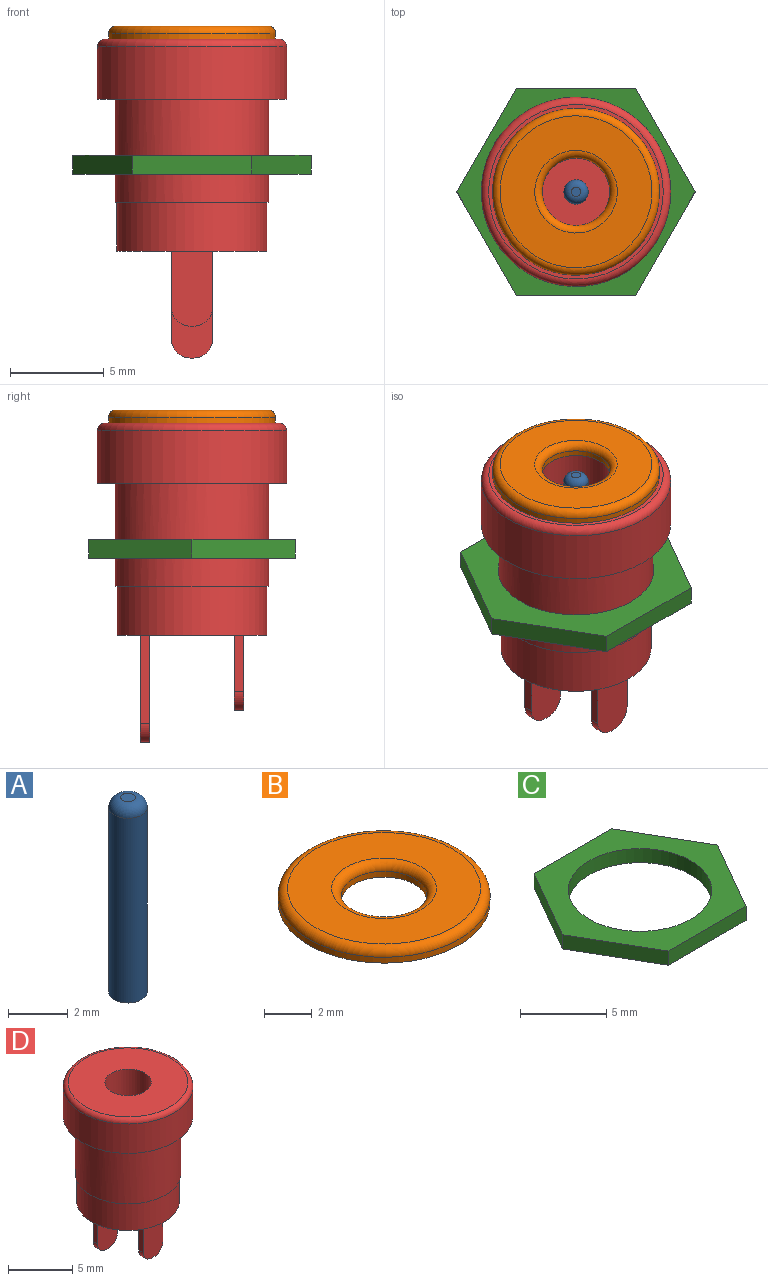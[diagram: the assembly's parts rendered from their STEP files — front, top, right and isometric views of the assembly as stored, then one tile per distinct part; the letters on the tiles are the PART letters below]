
ASSEMBLY  parts=4 mates=3
PART A: 4 faces, bbox 1.3x1.3x8 mm
  f0: cylinder r=0.65mm len=7.6mm, axis (0,0,1), area 31mm2, adj f1,f3
  f1: plane 1.3x1.3mm, normal (0,0,-1), area 1.3mm2, adj f0
  f2: plane 0.5x0.5mm, normal (0,0,1), area 0.2mm2, adj f3
  f3: torus R=0.25mm, axis (0,0,1), area 2mm2, adj f0,f2
PART B: 6 faces, bbox 9.6x9.6x0.7 mm
  f0: cylinder r=1.8mm len=3.6mm, axis (0,0,1), area 3.4mm2, adj f2,f4
  f1: cylinder r=4.45mm len=8.9mm, axis (0,0,1), area 8.4mm2, adj f2,f5
  f2: plane 8.9x8.9mm, normal (0,0,-1), area 52mm2, adj f0,f1
  f3: plane 8.1x8.1mm, normal (0,0,1), area 36.3mm2, adj f4,f5
  f4: torus R=2.2mm, axis (0,0,1), area 7.7mm2, adj f0,f3
  f5: torus R=4.05mm, axis (0,0,1), area 17mm2, adj f1,f3
PART C: 9 faces, bbox 12.7x11x1 mm
  f0: plane 5.5x3.18mm, normal (0.87,-0.5,0), area 6.4mm2, adj f1,f6,f7,f8
  f1: plane 5.5x3.18mm, normal (0.87,0.5,0), area 6.4mm2, adj f0,f2,f7,f8
  f2: plane 6.35x1mm, normal (0,1,0), area 6.4mm2, adj f1,f3,f7,f8
  f3: plane 5.5x3.18mm, normal (-0.87,0.5,0), area 6.4mm2, adj f2,f4,f7,f8
  f4: plane 5.5x3.18mm, normal (-0.87,-0.5,0), area 6.4mm2, adj f3,f6,f7,f8
  f5: cylinder r=4.15mm len=8.3mm, axis (0,0,-1), area 26.1mm2, adj f7,f8
  f6: plane 6.35x1mm, normal (0,-1,0), area 6.4mm2, adj f0,f4,f7,f8
  f7: plane 12.7x11mm, normal (0,0,1), area 50.7mm2, adj f0,f1,f2,f3,f4,f5,f6
  f8: plane 12.7x11mm, normal (0,0,-1), area 50.7mm2, adj f0,f1,f2,f3,f4,f5,f6
PART D: 24 faces, bbox 10.9x10.9x17 mm
  f0: plane 8x8mm, normal (0,0,-1), area 48.1mm2, adj f6,f7,f8,f9,f10,f12,f13,f14
  f1: cylinder r=5.05mm len=10.1mm, axis (0,0,-1), area 88.8mm2, adj f3,f19
  f2: plane 9.3x9.3mm, normal (0,0,1), area 57.8mm2, adj f17,f19
  f3: plane 10.1x10.1mm, normal (0,0,-1), area 27.3mm2, adj f1,f4
  f4: cylinder r=4.1mm len=8.2mm, axis (0,0,1), area 141.7mm2, adj f3,f5
  f5: plane 8.2x8.2mm, normal (0,0,-1), area 2.5mm2, adj f4,f6
  f6: cylinder r=4mm len=8mm, axis (0,0,1), area 65.3mm2, adj f0,f5
  f7: plane 4x2.2mm, normal (0,-1,0), area 8.4mm2, adj f0,f8,f10,f11,f22,f23
  f8: plane 3x0.5mm, normal (-1,0,0), area 1.5mm2, adj f0,f7,f9,f22
  f9: plane 4x2.2mm, normal (0,1,0), area 8.4mm2, adj f0,f8,f10,f11,f22,f23
  f10: plane 3x0.5mm, normal (1,0,0), area 1.5mm2, adj f0,f7,f9,f23
  f11: plane 0.5x0.2mm, normal (0,0,-1), area 0.1mm2, adj f7,f9,f22,f23
  f12: plane 5.7x2.2mm, normal (0,1,0), area 12.1mm2, adj f0,f13,f15,f16,f20,f21
  f13: plane 4.7x0.5mm, normal (1,0,0), area 2.4mm2, adj f0,f12,f14,f20
  f14: plane 5.7x2.2mm, normal (0,-1,0), area 12.1mm2, adj f0,f13,f15,f16,f20,f21
  f15: plane 4.7x0.5mm, normal (-1,0,0), area 2.4mm2, adj f0,f12,f14,f21
  f16: plane 0.5x0.2mm, normal (0,0,-1), area 0.1mm2, adj f12,f14,f20,f21
  f17: cylinder r=1.8mm len=10.2mm, axis (0,0,1), area 115.4mm2, adj f2,f18
  f18: plane 3.6x3.6mm, normal (0,0,1), area 10.2mm2, adj f17
  f19: torus R=4.65mm, axis (0,0,1), area 19.4mm2, adj f1,f2
  f20: cylinder r=1mm len=1mm, axis (0,1,0), area 0.8mm2, adj f12,f13,f14,f16
  f21: cylinder r=1mm len=1mm, axis (0,-1,0), area 0.8mm2, adj f12,f14,f15,f16
  f22: cylinder r=1mm len=1mm, axis (0,-1,0), area 0.8mm2, adj f7,f8,f9,f11
  f23: cylinder r=1mm len=1mm, axis (0,1,0), area 0.8mm2, adj f7,f9,f10,f11
PLACE A t=(0,0,7.3)mm
PLACE B t=(0,0,8)mm
PLACE C rot(axis=(1,0,0),180deg) t=(0,0,2.1)mm
PLACE D t=(0,0,8.1)mm
MATE fastened C.f5 <-> D.f1  axis (0,0,1) through (0,0,5.1)mm
MATE fastened D.f17 <-> A.f0  axis (0,0,1) through (0,0,11.3)mm
MATE fastened D.f17 <-> B.f0  axis (0,0,1) through (0,0,11.3)mm
